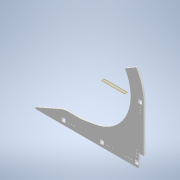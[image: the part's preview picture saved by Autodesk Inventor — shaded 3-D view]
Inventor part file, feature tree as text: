
AUTODESK INVENTOR PART (.ipt)
format: ipt  version: 2020 (Build 240168000, 168)  size: 322,048 bytes
history: native  units: in
note: dims shown in document units (in); Inventor stores cm internally (conversion verified against a paired STEP export)
features: reference x18, other x12, sketch x4, extrude x3, plane x1, fillet x1, revolve x1
ambient origin geometry x8: Origin, YZ Plane, XZ Plane, XY Plane, X Axis, Y Axis, Z Axis, Center Point
bodies: Solid1 (feature_tree)
feature tree (40):
  extrude  "Extrusion1"  Depth=16.0in
  plane  "Work Plane1"
  fillet  "Fillet3"  [1 undecoded]
  revolve  "Revolution2"  [1 undecoded]
  extrude  "Extrusion2"  Depth=1.0in
  extrude  "Extrusion3"  Depth=11.5in
  sketch  "Sketch1"  dims[d0=24.5in d1=16.0in d2=30.0deg]
  reference  "Reference1"
  sketch  "Sketch3"  dims[d4=16.0in d5=0.5in d6=0.0in]
  reference  "Reference3"
  sketch  "Sketch4"  dims[d7=1.0in d8=1.0in]
  reference  "Reference4"
  reference  "Reference5"
  reference  "Reference6"
  reference  "Reference7"
  reference  "Reference8"
  reference  "Reference9"
  reference  "Reference10"
  reference  "Reference11"
  reference  "Reference12"
  reference  "Reference13"
  reference  "Reference14"
  reference  "Reference15"
  sketch  "Sketch5"  dims[d9=1.5in d10=11.5in d16=16.0in d17=1.0in d18=7.0in d19=9.5in d20=90.0deg d21=1.0in d22=1.0in d23=1.0in d24=0.0in d25=0.0in d27=0.75in d32=4.0in d33=4.0in d34=5.0in d35=0.25in d36=0.0in d37=0.0in d40=10.0in d41=5.0in]
  reference  "Reference16"
  reference  "Reference17"
  reference  "Reference18"
  reference  "Reference19"
  other  "<userpath>\Documents\FRC\2020\IntakeShooter\IndexerA.iam"
  other  "IndexerA.iam"
  other  "CenterIndexerWheel:1"
  other  "IndexerSpacer5_5:3"
  other  "IndexerSpacer5_5:4"
  other  "IndexerSpacer5_5:1"
  other  "IndexerSpacer5_5:2"
  other  "<userpath>\Documents\FRC\2020\Prototype1.iam"
  other  "Prototype1.iam"
  other  "DriveBase2020:1"
  other  "AM14U3 End Sheet Square:2"
  other  "IndexerSpacer5_5_2:1"
note: 2 required parameter values undecoded (feature->parameter linkage not recoverable at this tier; creation-order binding heuristic only, values carry confidence <= 0.55)